FCSTD DOCUMENT  (FreeCAD 0.19R)
Label: tangent
License: All rights reserved
LicenseURL: http://en.wikipedia.org/wiki/All_rights_reserved
objects: Sketcher::SketchObject×1, PartDesign::Body×1
note: 2 computed .brp shape members not serialized (recipe doc carries the construction recipe); baked Part::Feature solids carry a one-line shape summary decoded from their .brp

FEATURE [Sketcher::SketchObject] Sketch
  MapMode = 5
  Support = -> [XY_Plane]
  sketch-geometry (10):
    g0: LineSegment StartX=-38.7039 StartY=38.3635 StartZ=0 EndX=45.2961 EndY=-25.6365 EndZ=0
    g1: LineSegment StartX=40.4477 StartY=-40 StartZ=0 EndX=-43.5523 EndY=-40 EndZ=0
    g2: LineSegment StartX=-51.5523 StartY=-32 StartZ=0 EndX=-51.5523 EndY=32 EndZ=0
    g3: ArcOfCircle CenterX=-43.5523 CenterY=32 CenterZ=0 NormalX=0 NormalY=0 NormalZ=1 AngleXU=0 Radius=8 StartAngle=0.91972 EndAngle=3.14159
    g4: ArcOfCircle CenterX=-43.5523 CenterY=-32 CenterZ=0 NormalX=0 NormalY=0 NormalZ=1 AngleXU=0 Radius=8 StartAngle=3.14159 EndAngle=4.71239
    g5: ArcOfCircle CenterX=40.4477 CenterY=-32 CenterZ=0 NormalX=0 NormalY=0 NormalZ=1 AngleXU=0 Radius=8 StartAngle=4.71239 EndAngle=7.2029
    g6: LineSegment [constr] StartX=48.4477 StartY=56.2673 StartZ=0 EndX=48.4477 EndY=-50.2775 EndZ=0
    g7: LineSegment [constr] StartX=48.4477 StartY=-50.2775 StartZ=0 EndX=-51.5523 EndY=-50.2775 EndZ=0
    g8: LineSegment [constr] StartX=-51.5523 StartY=-50.2775 StartZ=0 EndX=-51.5523 EndY=56.2673 EndZ=0
    g9: LineSegment [constr] StartX=40.4477 StartY=-32 StartZ=0 EndX=48.4477 EndY=-32 EndZ=0
  constraints (22):
    c: Tangent(g0,g3) = 1.5708
    c: Tangent(g2,g3) = 1.5708
    c: Tangent(g1,g4) = 1.5708
    c: Tangent(g2,g4) = 1.5708
    c: Tangent(g0,g5) = 1.5708
    c: Tangent(g1,g5) = 1.5708
    c: Horizontal(g1)
    c: Equal(g4,g3)
    c: Radius(g3) = 8
    c: Symmetric(g2,g2,g-1)
    c: DistanceY(g2,g2) = 64
    c: Coincident(g6,g7)
    c: Coincident(g7,g8)
    c: Horizontal(g7)
    c: Vertical(g6)
    c: Tangent(g8,g2)
    c: DistanceX(g7,g7) = 100
    c: Coincident(g9,g5)
    c: Horizontal(g9)
    c: PointOnObject(g9,g6)
    c: PointOnObject(g9,g5)
    c: Equal(g4,g5)
FEATURE [PartDesign::Body] Body
  Group = -> [Sketch]
  Origin = -> Origin
